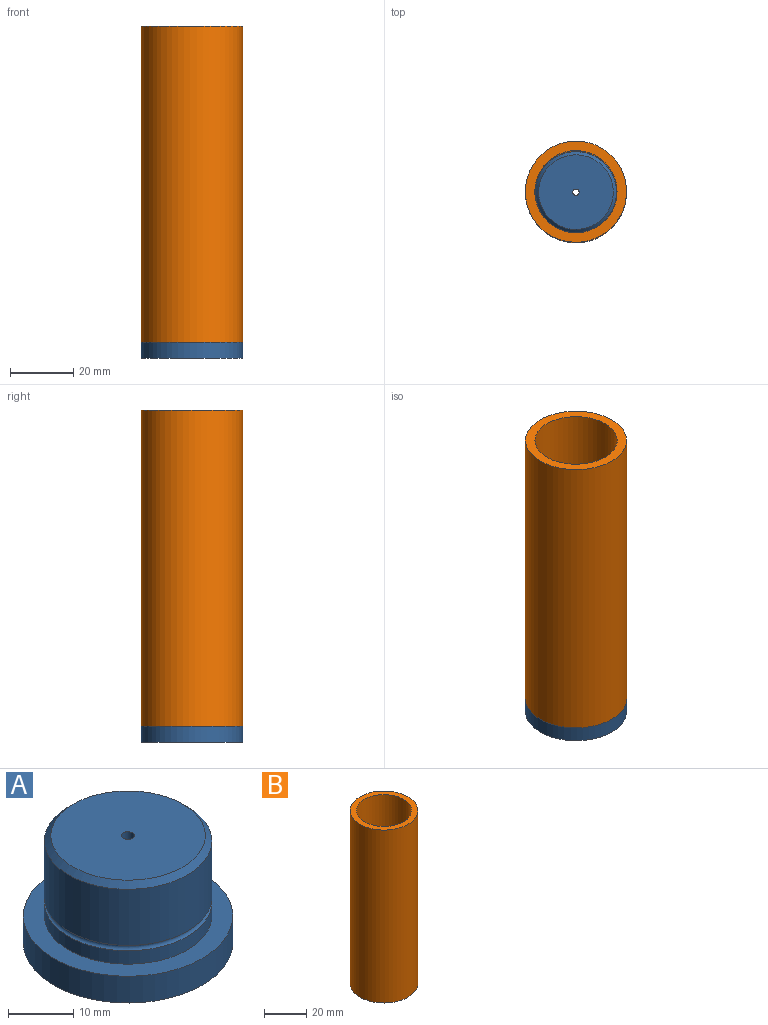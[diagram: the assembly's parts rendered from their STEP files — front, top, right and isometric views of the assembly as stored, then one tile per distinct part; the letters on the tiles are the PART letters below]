
ASSEMBLY  parts=2 mates=1
PART A: 14 faces, bbox 32x32x20 mm
  f0: cylinder r=1mm len=5mm, axis (0,0,1), area 31.4mm2, adj f1,f11
  f1: cone r=5mm half-angle=38.7deg, axis (0,0,-1), area 120.7mm2, adj f0,f2
  f2: cylinder r=5mm len=10mm, axis (0,0,1), area 204.2mm2, adj f1,f3
  f3: torus R=5mm, axis (0,0,1), area 52.5mm2, adj f2,f4
  f4: cylinder r=5mm len=10mm, axis (0,0,1), area 47.1mm2, adj f3,f13
  f5: plane 32x32mm, normal (0,0,-1), area 691.2mm2, adj f6,f13
  f6: cylinder r=16mm len=32mm, axis (0,0,1), area 502.7mm2, adj f5,f7
  f7: plane 32x32mm, normal (0,0,1), area 289.5mm2, adj f6,f8
  f8: cylinder r=12.8mm len=25.6mm, axis (0,0,1), area 201.1mm2, adj f7,f9
  f9: torus R=12.8mm, axis (0,0,1), area 123.2mm2, adj f8,f10
  f10: cylinder r=12.8mm len=25.6mm, axis (0,0,1), area 844.5mm2, adj f9,f12
  f11: plane 23.6x23.6mm, normal (0,0,1), area 434.3mm2, adj f0,f12
  f12: cone r=11.8mm half-angle=45deg, axis (0,0,-1), area 109.3mm2, adj f10,f11
  f13: cone r=6mm half-angle=45deg, axis (0,0,-1), area 48.9mm2, adj f4,f5
PART B: 4 faces, bbox 32x32x100 mm
  f0: cylinder r=13mm len=100mm, axis (0,0,-1), area 8168.1mm2, adj f2,f3
  f1: cylinder r=16mm len=100mm, axis (0,0,-1), area 10053.1mm2, adj f2,f3
  f2: plane 32x32mm, normal (0,0,1), area 273.3mm2, adj f0,f1
  f3: plane 32x32mm, normal (0,0,-1), area 273.3mm2, adj f0,f1
PLACE A t=(0,0,-85)mm
PLACE B t=(0,0,-100)mm
MATE revolute A.f0 <-> B.f0  axis (0,0,1) through (0,0,-100)mm
